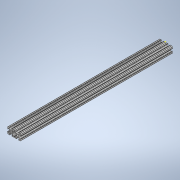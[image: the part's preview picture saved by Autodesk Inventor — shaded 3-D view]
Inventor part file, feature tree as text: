
AUTODESK INVENTOR PART (.ipt)
format: ipt  version: 2020 (Build 240168000, 168)  size: 332,800 bytes
history: native  units: in
note: dims shown in document units (in); Inventor stores cm internally (conversion verified against a paired STEP export)
features: sketch x2, extrude x1
ambient origin geometry x8: Origin, YZ Plane, XZ Plane, XY Plane, X Axis, Y Axis, Z Axis, Center Point
bodies: Solid1 (feature_tree)
feature tree (3):
  extrude  "Extrusion1"  [1 undecoded]
  sketch  "Sketch2"
  sketch  "Sketch1"  dims[d0=23.0in d1=0.0in]
note: 1 required parameter value undecoded (feature->parameter linkage not recoverable at this tier; creation-order binding heuristic only, values carry confidence <= 0.55)
